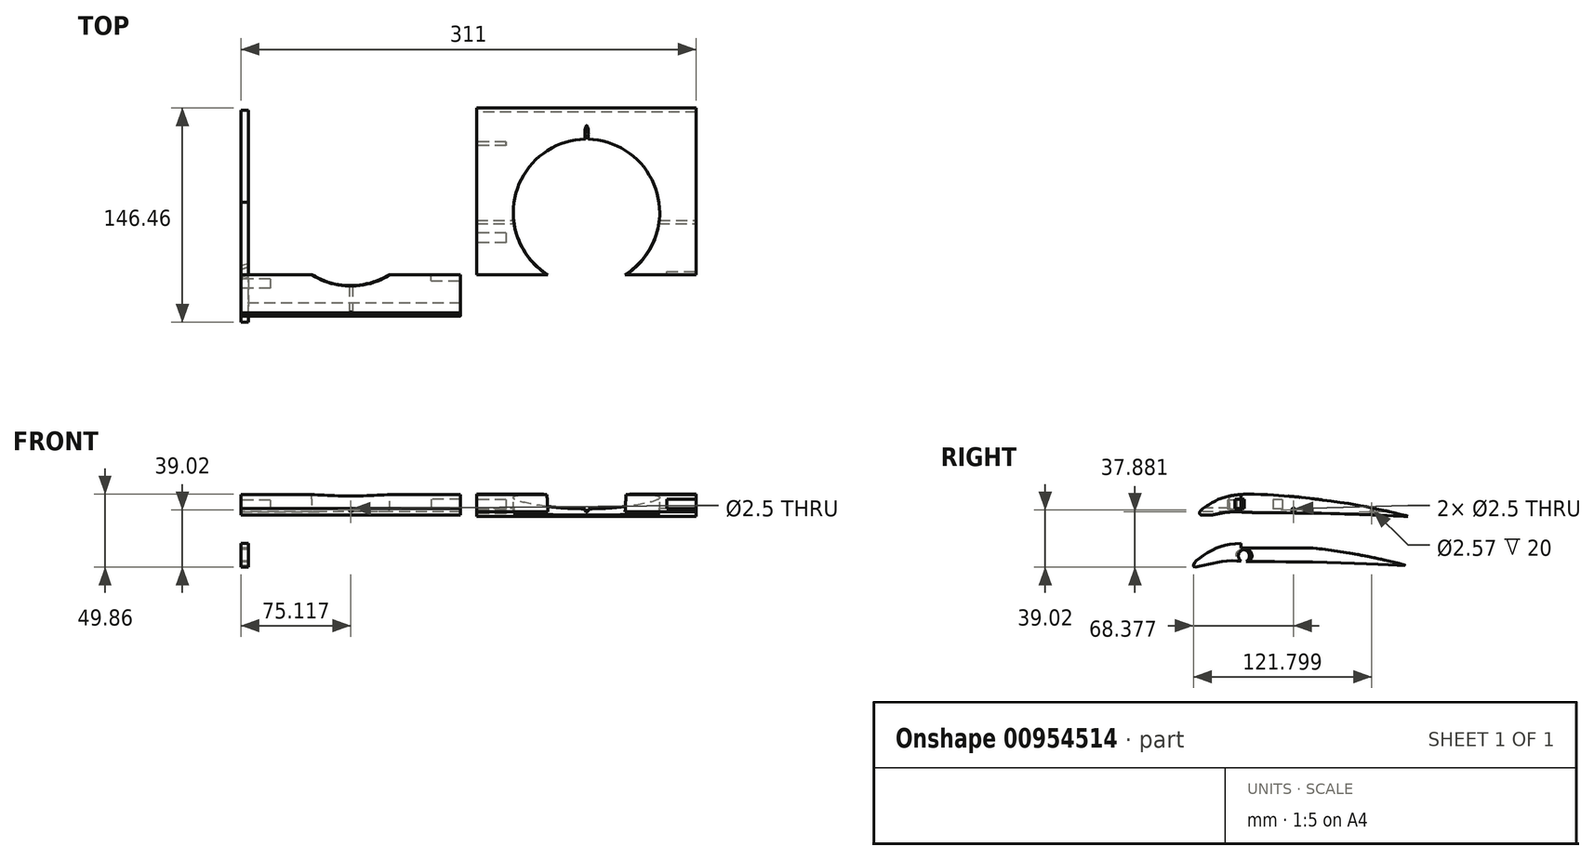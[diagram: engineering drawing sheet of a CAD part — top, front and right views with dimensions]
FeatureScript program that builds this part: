
annotation { "Feature Type Name" : "Feature", "Feature Type Description" : "" }
export const myFeature = defineFeature(function(context is Context, id is Id, definition is map)
    precondition{}
    {
        {
            var Q0;
            Q0=qCreatedBy(makeId("Right.planeOp"),FACE);
            var sketch = newSketch(context, id + "F0", { "sketchPlane" : qUnion([Q0])});
            skFitSpline(sketch, "E0", {"points": [v(-58.33, -12) * mm, v(-57.57, -10.15) * mm, v(-53.53, -6.54) * mm, v(-44.02, -0.73) * mm, v(-35.1, 2.13) * mm, v(-21.3, 3.4) * mm, v(-6.08, 2.72) * mm, v(5.45, 1.96) * mm, v(29.18, -0.73) * mm, v(57.79, -5.19) * mm, v(83.53, -10.91) * mm, v(86.48, -11.84) * mm, v(84.04, -11.84) * mm, v(70.58, -11.16) * mm, v(43.9, -10.15) * mm, v(9.07, -9.48) * mm, v(-12.22, -9.23) * mm, v(-22.65, -9.06) * mm, v(-33.42, -8.72) * mm, v(-43.43, -10.07) * mm, v(-52.19, -12.09) * mm, v(-57.74, -12.93) * mm, v(-58.33, -12) * mm]});
            skLineSegment(sketch, "E1", {"start": v(-28.6, -8.75) * mm, "end": v(-24.93, -8.94) * mm});
            skSolve(sketch);
        }
        {
            var Q0;
            Q0=makeQuery(id+"F0.imprint","IMPRINT",FACE,{"disambiguationData":[TD([[makeQuery(id+"F0.imprint","IMPRINT",EDGE,{"derivedFrom":sQuery(id+"F0.wireOp",EDGE,"E0")}),-1.0]])]});
            extrude(context, id + "F1", {"entities" : qUnion([Q0]), "depth" : 5 * mm, "offsetDistance" : 25 * mm});
        }
        {
            var Q0;
            Q0=qCreatedBy(makeId("Top.planeOp"),FACE);
            var sketch = newSketch(context, id + "F2", { "sketchPlane" : qUnion([Q0])});
            skLineSegment(sketch, "E2", {"start": v(10.1, -34.69) * mm, "end": v(4.1, -36.87) * mm});
            skLineSegment(sketch, "E3", {"start": v(10.1, -34.69) * mm, "end": v(4.1, -34.69) * mm, "construction": true});
            skLineSegment(sketch, "E4", {"start": v(4.1, -34.69) * mm, "end": v(4.1, -36.87) * mm, "construction": true});
            skSolve(sketch);
        }
        {
            var Q0;
            Q0=sQuery(id+"F2.wireOp",EDGE,"E2");
            var Q1;
            Q1=sQuery(id+"F2.wireOp",VERTEX,"E2.start");
            cPlane(context, id + "F3", {"entities" : qUnion([Q0, Q1]), "cplaneType" : CPlaneType.LINE_POINT, "offset" : 25 * mm, "width" : 150 * mm, "height" : 150 * mm});
        }
        {
            var Q0;
            Q0=qCreatedBy(id+"F3.planeOp",FACE);
            var sketch = newSketch(context, id + "F4", { "sketchPlane" : qUnion([Q0])});
            skCircle(sketch, "E5", {"center": v(23.29, -5.36) * mm, "radius": 4.4 * mm});
            skSolve(sketch);
        }
        {
            var Q0;
            Q0 = qSketchRegion(id + "F4", true);
            extrude(context, id + "F5", {"entities" : qUnion([Q0]), "operationType" : NewBodyOperationType.REMOVE, "oppositeDirection" : true, "depth" : 25 * mm, "offsetDistance" : 25 * mm, "hasSecondDirection" : true, "secondDirectionOppositeDirection" : false, "secondDirectionDepth" : 25 * mm});
        }
        {
            var Q0;
            Q0=qCreatedBy(makeId("Right.planeOp"),FACE);
            var sketch = newSketch(context, id + "F6", { "sketchPlane" : qUnion([Q0])});
            skLineSegment(sketch, "E6", {"start": v(88.13, 21.59) * mm, "end": v(-53.49, 22.66) * mm});
            skFitSpline(sketch, "E7", {"points": [v(-51.88, 26.89) * mm, v(-54.06, 24.54) * mm, v(-54.06, 23.32) * mm, v(-53.49, 22.66) * mm], "startDerivative": vector(-5.98, -5.17) * mm, "endDerivative": vector(2.7, -2.39) * mm});
            skFitSpline(sketch, "E8.trimOffspring", {"points": [v(-56.68, 21.42) * mm, v(-55.92, 23.27) * mm, v(-51.88, 26.89) * mm, v(-42.37, 32.7) * mm, v(-33.46, 35.56) * mm, v(-19.66, 36.82) * mm, v(-4.43, 36.14) * mm, v(7.1, 35.39) * mm, v(30.83, 32.7) * mm, v(59.44, 28.24) * mm, v(85.18, 22.51) * mm, v(88.13, 21.59) * mm, v(85.69, 21.59) * mm, v(72.22, 22.26) * mm, v(45.55, 23.27) * mm, v(10.72, 23.94) * mm, v(-10.57, 24.2) * mm, v(-21, 24.36) * mm, v(-31.77, 24.7) * mm, v(-41.79, 23.36) * mm, v(-50.54, 21.34) * mm, v(-56.09, 20.5) * mm, v(-56.68, 21.42) * mm]});
            skSolve(sketch);
        }
        {
            var Q0;
            Q0=makeQuery(id+"F6.imprint","IMPRINT",FACE,{"disambiguationData":[TD([[makeQuery(id+"F6.imprint","IMPRINT",EDGE,{"derivedFrom":sQuery(id+"F6.wireOp",EDGE,"E6")}),-1.0]])]});
            extrude(context, id + "F7", {"entities" : qUnion([Q0]), "depth" : 150 * mm, "offsetDistance" : 25 * mm});
        }
        {
            var Q0;
            Q0=qCreatedBy(makeId("Right.planeOp"),FACE);
            var sketch = newSketch(context, id + "F8", { "sketchPlane" : qUnion([Q0])});
            skLineSegment(sketch, "E9", {"start": v(-54.05, 28.47) * mm, "end": v(74.15, 28.47) * mm, "construction": true});
            skLineSegment(sketch, "E10", {"start": v(10.05, 28.47) * mm, "end": v(10.05, 73.47) * mm, "construction": true});
            skLineSegment(sketch, "E11", {"start": v(10.05, 73.47) * mm, "end": v(8.55, 73.47) * mm, "construction": true});
            skLineSegment(sketch, "E12", {"start": v(10.05, 28.47) * mm, "end": v(8.55, 73.47) * mm});
            skSolve(sketch);
        }
        {
            var Q0;
            Q0=sQuery(id+"F8.wireOp",VERTEX,"E11.end");
            var Q1;
            Q1=sQuery(id+"F8.wireOp",EDGE,"E12");
            cPlane(context, id + "F9", {"entities" : qUnion([Q0, Q1]), "cplaneType" : CPlaneType.LINE_POINT, "offset" : 25 * mm, "width" : 150 * mm, "height" : 150 * mm});
        }
        {
            var Q0;
            Q0=qCreatedBy(id+"F9.planeOp",FACE);
            var sketch = newSketch(context, id + "F10", { "sketchPlane" : qUnion([Q0])});
            skLineSegment(sketch, "E13", {"start": v(0, 17.49) * mm, "end": v(150, 17.49) * mm, "construction": true});
            skLineSegment(sketch, "E14", {"start": v(150, 17.49) * mm, "end": v(150, 78) * mm, "construction": true});
            skLineSegment(sketch, "E15", {"start": v(150, 17.49) * mm, "end": v(150, -43.03) * mm, "construction": true});
            skPoint(sketch, "E16", {"position": v(75, 17.49) * mm});
            skCircle(sketch, "E17", {"center": v(75, 17.49) * mm, "radius": 50 * mm});
            skSolve(sketch);
        }
        {
            var Q0;
            Q0=makeQuery(id+"F10.imprint","IMPRINT",FACE,{"disambiguationData":[TD([[makeQuery(id+"F10.imprint","IMPRINT",EDGE,{"derivedFrom":sQuery(id+"F10.wireOp",EDGE,"E17")}),1.0]])]});
            extrude(context, id + "F11", {"entities" : qUnion([Q0]), "operationType" : NewBodyOperationType.REMOVE, "oppositeDirection" : true, "depth" : 79 * mm, "offsetDistance" : 25 * mm});
        }
        {
            var Q0;
            Q0=sQuery(id+"F8.wireOp",EDGE,"E12");
            var Q1;
            Q1=sQuery(id+"F8.wireOp",VERTEX,"E10.start");
            cPlane(context, id + "F12", {"entities" : qUnion([Q0, Q1]), "cplaneType" : CPlaneType.LINE_POINT, "offset" : 25 * mm, "width" : 150 * mm, "height" : 150 * mm});
        }
        {
            var Q0;
            Q0=qCreatedBy(id+"F12.planeOp",FACE);
            var sketch = newSketch(context, id + "F13", { "sketchPlane" : qUnion([Q0])});
            skCircle(sketch, "E18", {"center": v(75.12, 17.9) * mm, "radius": 49.93 * mm});
            skSolve(sketch);
        }
        {
            var Q0;
            Q0=sQuery(id+"F13.wireOp",VERTEX,"E18.center");
            var Q1;
            Q1=qCreatedBy(makeId("Right.planeOp"),FACE);
            cPlane(context, id + "F14", {"entities" : qUnion([Q0, Q1]), "cplaneType" : CPlaneType.PLANE_POINT, "offset" : 25 * mm, "width" : 150 * mm, "height" : 150 * mm});
        }
        {
            var Q0;
            Q0=qCreatedBy(id+"F14.planeOp",FACE);
            var sketch = newSketch(context, id + "F15", { "sketchPlane" : qUnion([Q0])});
            skPoint(sketch, "E19", {"position": v(10.05, 25.98) * mm});
            skCircle(sketch, "E20", {"center": v(10.05, 25.98) * mm, "radius": 1.25 * mm});
            skSolve(sketch);
        }
        {
            var Q0;
            Q0=sQuery(id+"F15.wireOp",VERTEX,"E19");
            var Q1;
            Q1=qCreatedBy(makeId("Front.planeOp"),FACE);
            cPlane(context, id + "F16", {"entities" : qUnion([Q0, Q1]), "cplaneType" : CPlaneType.PLANE_POINT, "offset" : 25 * mm, "width" : 150 * mm, "height" : 150 * mm});
        }
        {
            var Q0;
            Q0=qCreatedBy(id+"F16.planeOp",FACE);
            var sketch = newSketch(context, id + "F17", { "sketchPlane" : qUnion([Q0])});
            skCircle(sketch, "E21", {"center": v(75.12, 25.98) * mm, "radius": 1.25 * mm});
            skSolve(sketch);
        }
        {
            var Q0;
            Q0=makeQuery(id+"F15.imprint","IMPRINT",FACE,{"disambiguationData":[TD([[makeQuery(id+"F15.imprint","IMPRINT",EDGE,{"derivedFrom":sQuery(id+"F15.wireOp",EDGE,"E20")}),1.0]])]});
            extrude(context, id + "F18", {"entities" : qUnion([Q0]), "operationType" : NewBodyOperationType.REMOVE, "oppositeDirection" : true, "depth" : 81 * mm, "offsetDistance" : 25 * mm, "hasSecondDirection" : true, "secondDirectionOppositeDirection" : false, "secondDirectionDepth" : 95 * mm});
        }
        {
            var Q0;
            Q0=makeQuery(id+"F17.imprint","IMPRINT",FACE,{"disambiguationData":[TD([[makeQuery(id+"F17.imprint","IMPRINT",EDGE,{"derivedFrom":sQuery(id+"F17.wireOp",EDGE,"E21")}),1.0]])]});
            extrude(context, id + "F19", {"entities" : qUnion([Q0]), "operationType" : NewBodyOperationType.REMOVE, "oppositeDirection" : true, "depth" : 79.7 * mm, "offsetDistance" : 25 * mm, "hasSecondDirection" : true, "secondDirectionOppositeDirection" : false, "secondDirectionDepth" : 89.9 * mm});
        }
        {
            var Q0;
            Q0=makeQuery(id+"F7.opExtrude","CAP_FACE",FACE,{"disambiguationData":[OSD([sQuery(id+"F6.wireOp",EDGE,"E6"),sQuery(id+"F6.wireOp",EDGE,"E7"),sQuery(id+"F6.wireOp",EDGE,"E8.trimOffspring")])],"isStart":false});
            var sketch = newSketch(context, id + "F20", { "sketchPlane" : qUnion([Q0])});
            skLineSegment(sketch, "E22.bottom", {"start": v(-30.1, 33.37) * mm, "end": v(-23.7, 33.37) * mm});
            skLineSegment(sketch, "E22.top", {"start": v(-30.1, 26.97) * mm, "end": v(-23.7, 26.97) * mm});
            skLineSegment(sketch, "E22.left", {"start": v(-30.1, 33.37) * mm, "end": v(-30.1, 26.97) * mm});
            skLineSegment(sketch, "E22.right", {"start": v(-23.7, 33.37) * mm, "end": v(-23.7, 26.97) * mm});
            skSolve(sketch);
        }
        {
            var Q0;
            Q0=makeQuery(id+"F20.imprint","IMPRINT",FACE,{"disambiguationData":[TD([[makeQuery(id+"F20.imprint","IMPRINT",EDGE,{"derivedFrom":sQuery(id+"F20.wireOp",EDGE,"E22.bottom")}),-1.0]])]});
            extrude(context, id + "F21", {"entities" : qUnion([Q0]), "operationType" : NewBodyOperationType.REMOVE, "oppositeDirection" : true, "depth" : 20 * mm, "offsetDistance" : 25 * mm});
        }
        {
            var Q0;
            Q0=makeQuery(id+"F7.opExtrude","CAP_FACE",FACE,{"disambiguationData":[OSD([sQuery(id+"F6.wireOp",EDGE,"E6"),sQuery(id+"F6.wireOp",EDGE,"E7"),sQuery(id+"F6.wireOp",EDGE,"E8.trimOffspring")])],"isStart":true});
            var sketch = newSketch(context, id + "F22", { "sketchPlane" : qUnion([Q0])});
            skLineSegment(sketch, "E23.bottom", {"start": v(28.75, 32.73) * mm, "end": v(35.15, 32.73) * mm});
            skLineSegment(sketch, "E23.top", {"start": v(28.75, 26.33) * mm, "end": v(35.15, 26.33) * mm});
            skLineSegment(sketch, "E23.left", {"start": v(28.75, 32.73) * mm, "end": v(28.75, 26.33) * mm});
            skLineSegment(sketch, "E23.right", {"start": v(35.15, 32.73) * mm, "end": v(35.15, 26.33) * mm});
            skLineSegment(sketch, "E24.bottom", {"start": v(-2.47, 32.94) * mm, "end": v(3.93, 32.94) * mm});
            skLineSegment(sketch, "E24.top", {"start": v(-2.47, 26.54) * mm, "end": v(3.93, 26.54) * mm});
            skLineSegment(sketch, "E24.left", {"start": v(-2.47, 32.94) * mm, "end": v(-2.47, 26.54) * mm});
            skLineSegment(sketch, "E24.right", {"start": v(3.93, 32.94) * mm, "end": v(3.93, 26.54) * mm});
            skCircle(sketch, "E25", {"center": v(-63.47, 24.84) * mm, "radius": 1.28 * mm});
            skSolve(sketch);
        }
        {
            var Q0;
            Q0=makeQuery(id+"F22.imprint","IMPRINT",FACE,{"disambiguationData":[TD([[makeQuery(id+"F22.imprint","IMPRINT",EDGE,{"derivedFrom":sQuery(id+"F22.wireOp",EDGE,"E24.bottom")}),-1.0]])]});
            var Q1;
            Q1=makeQuery(id+"F22.imprint","IMPRINT",FACE,{"disambiguationData":[TD([[makeQuery(id+"F22.imprint","IMPRINT",EDGE,{"derivedFrom":sQuery(id+"F22.wireOp",EDGE,"E25")}),1.0]])]});
            var Q2;
            Q2=makeQuery(id+"F22.imprint","IMPRINT",FACE,{"disambiguationData":[TD([[makeQuery(id+"F22.imprint","IMPRINT",EDGE,{"derivedFrom":sQuery(id+"F22.wireOp",EDGE,"E23.bottom")}),-1.0]])]});
            extrude(context, id + "F23", {"entities" : qUnion([Q0, Q1, Q2]), "operationType" : NewBodyOperationType.REMOVE, "oppositeDirection" : true, "depth" : 20 * mm, "offsetDistance" : 25 * mm});
        }
        {
            var Q0;
            Q0=makeQuery(id+"F7.opExtrude","SWEPT_BODY",BODY,{"disambiguationData":[OSD([sQuery(id+"F6.wireOp",EDGE,"E6"),sQuery(id+"F6.wireOp",EDGE,"E7"),sQuery(id+"F6.wireOp",EDGE,"E8.trimOffspring")])]});
            transform(context, id + "F24", {"entities" : qUnion([Q0]), "transformType" : TransformType.TRANSLATION_3D, "dx" : 161 * mm, "dy" : 0 * mm, "dz" : 0 * mm, "makeCopy" : true});
        }
        {
            var Q0;
            Q0=qCreatedBy(makeId("Top.planeOp"),FACE);
            var sketch = newSketch(context, id + "F25", { "sketchPlane" : qUnion([Q0])});
            skLineSegment(sketch, "E26.bottom", {"start": v(154.06, -25.82) * mm, "end": v(-12.21, -25.82) * mm});
            skLineSegment(sketch, "E26.top", {"start": v(154.06, 98.75) * mm, "end": v(-12.21, 98.75) * mm});
            skLineSegment(sketch, "E26.left", {"start": v(154.06, -25.82) * mm, "end": v(154.06, 98.75) * mm});
            skLineSegment(sketch, "E26.right", {"start": v(-12.21, -25.82) * mm, "end": v(-12.21, 98.75) * mm});
            skLineSegment(sketch, "E27.bottom", {"start": v(154.06, -25.82) * mm, "end": v(350.25, -25.82) * mm});
            skLineSegment(sketch, "E27.top", {"start": v(154.06, -77.66) * mm, "end": v(350.25, -77.66) * mm});
            skLineSegment(sketch, "E27.left", {"start": v(154.06, -25.82) * mm, "end": v(154.06, -77.66) * mm});
            skLineSegment(sketch, "E27.right", {"start": v(350.25, -25.82) * mm, "end": v(350.25, -77.66) * mm});
            skSolve(sketch);
        }
        {
            var Q0;
            Q0=makeQuery(id+"F25.imprint","IMPRINT",FACE,{"disambiguationData":[TD([[makeQuery(id+"F25.imprint","IMPRINT",EDGE,{"derivedFrom":sQuery(id+"F25.wireOp",EDGE,"E26.bottom")}),-1.0]])]});
            extrude(context, id + "F26", {"entities" : qUnion([Q0]), "operationType" : NewBodyOperationType.REMOVE, "depth" : 80 * mm, "offsetDistance" : 25 * mm});
        }
        {
            var Q0;
            Q0=makeQuery(id+"F25.imprint","IMPRINT",FACE,{"disambiguationData":[TD([[makeQuery(id+"F25.imprint","IMPRINT",EDGE,{"derivedFrom":sQuery(id+"F25.wireOp",EDGE,"E27.bottom")}),-1.0]])]});
            extrude(context, id + "F27", {"entities" : qUnion([Q0]), "operationType" : NewBodyOperationType.REMOVE, "depth" : 80 * mm, "offsetDistance" : 25 * mm});
        }
    });
